FCSTD DOCUMENT  (FreeCAD 1.0R39319 (Git))
Label: arm3
License: All rights reserved
LicenseURL: https://en.wikipedia.org/wiki/All_rights_reserved
objects: Sketcher::SketchObject×1, PartDesign::Body×1
note: 3 computed .brp shape members not serialized (recipe doc carries the construction recipe); baked Part::Feature solids carry a one-line shape summary decoded from their .brp

FEATURE [Sketcher::SketchObject] Sketch
  ArcFitTolerance = 1e-06
  AttachmentSupport = -> [XY_Plane]
  FullyConstrained = false
  MakeInternals = false
  MapMode = 5
  sketch-geometry (162):
    g0: LineSegment [constr] StartX=20.0632 StartY=2.83397e-05 StartZ=0 EndX=20.0632 EndY=-40 EndZ=0
    g1: Circle [constr] CenterX=20.0632 CenterY=-20 CenterZ=0 NormalX=0 NormalY=0 NormalZ=1 AngleXU=0 Radius=14
    g2: LineSegment [constr] StartX=20.0632 StartY=-20 StartZ=0 EndX=20.0632 EndY=380 EndZ=0
    g3: LineSegment [constr] StartX=20.0632 StartY=2.83397e-05 StartZ=0 EndX=20.0632 EndY=5.00004 EndZ=0
    g4: Circle CenterX=20.0632 CenterY=380 CenterZ=0 NormalX=0 NormalY=0 NormalZ=1 AngleXU=0 Radius=5
    g5: LineSegment [constr] StartX=20.0632 StartY=-20 StartZ=0 EndX=-4.93685 EndY=-20 EndZ=0
    g6: LineSegment [constr] StartX=20.0632 StartY=-20 StartZ=0 EndX=45.0632 EndY=-20 EndZ=0
    g7: Circle CenterX=20.0632 CenterY=380 CenterZ=0 NormalX=0 NormalY=0 NormalZ=1 AngleXU=0 Radius=2
    g8: LineSegment [constr] StartX=120.063 StartY=-20 StartZ=0 EndX=120.063 EndY=380 EndZ=0
    g9: Circle CenterX=120.063 CenterY=380 CenterZ=0 NormalX=0 NormalY=0 NormalZ=1 AngleXU=0 Radius=5
    g10: Circle CenterX=120.063 CenterY=380 CenterZ=0 NormalX=0 NormalY=0 NormalZ=1 AngleXU=0 Radius=2
    g11: LineSegment [constr] StartX=120.063 StartY=3.7e-05 StartZ=0 EndX=120.063 EndY=-40 EndZ=0
    g12: Circle [constr] CenterX=120.063 CenterY=-20 CenterZ=0 NormalX=0 NormalY=0 NormalZ=1 AngleXU=0 Radius=14
    g13: LineSegment [constr] StartX=120.063 StartY=-20 StartZ=0 EndX=95.0632 EndY=-20 EndZ=0
    g14: Circle [constr] CenterX=20.0632 CenterY=-20.0003 CenterZ=0 NormalX=0 NormalY=0 NormalZ=1 AngleXU=0 Radius=11
    g15: LineSegment [constr] StartX=20.0632 StartY=-20 StartZ=0 EndX=20.0632 EndY=-9.00027 EndZ=0
    g16: Circle CenterX=20.0632 CenterY=-9.00027 CenterZ=0 NormalX=0 NormalY=0 NormalZ=1 AngleXU=0 Radius=1.25
    g17: Circle CenterX=9.06345 CenterY=-20 CenterZ=0 NormalX=0 NormalY=0 NormalZ=1 AngleXU=0 Radius=1.25
    g18: Circle CenterX=20.0632 CenterY=-30.9997 CenterZ=0 NormalX=0 NormalY=0 NormalZ=1 AngleXU=0 Radius=1.25
    g19: Circle CenterX=31.0629 CenterY=-20 CenterZ=0 NormalX=0 NormalY=0 NormalZ=1 AngleXU=0 Radius=1.25
    g20: LineSegment [constr] StartX=120.063 StartY=-20 StartZ=0 EndX=145.063 EndY=-20 EndZ=0
    g21: Circle [constr] CenterX=120.063 CenterY=-20.0003 CenterZ=0 NormalX=0 NormalY=0 NormalZ=1 AngleXU=0 Radius=11
    g22: Circle CenterX=131.063 CenterY=-20 CenterZ=0 NormalX=0 NormalY=0 NormalZ=1 AngleXU=0 Radius=1.25
    g23: Circle CenterX=120.063 CenterY=-9.00027 CenterZ=0 NormalX=0 NormalY=0 NormalZ=1 AngleXU=0 Radius=1.25
    g24: Circle CenterX=109.063 CenterY=-20 CenterZ=0 NormalX=0 NormalY=0 NormalZ=1 AngleXU=0 Radius=1.25
    g25: Circle CenterX=120.063 CenterY=-30.9997 CenterZ=0 NormalX=0 NormalY=0 NormalZ=1 AngleXU=0 Radius=1.25
    g26: LineSegment [constr] StartX=99.9621 StartY=66.1 StartZ=0 EndX=140.162 EndY=66.1 EndZ=0
    g27: LineSegment [constr] StartX=140.162 StartY=66.1 StartZ=0 EndX=140.162 EndY=5.00003 EndZ=0
    g28: LineSegment [constr] StartX=120.062 StartY=60.5 StartZ=0 EndX=134.562 EndY=60.5 EndZ=0
    g29: LineSegment StartX=134.562 StartY=60.5 StartZ=0 EndX=105.562 EndY=60.5 EndZ=0
    g30: LineSegment StartX=134.562 StartY=60.5 StartZ=0 EndX=134.562 EndY=5.00003 EndZ=0
    g31: Circle CenterX=131.062 CenterY=63.3 CenterZ=0 NormalX=0 NormalY=0 NormalZ=1 AngleXU=0 Radius=1.25
    g32: Circle CenterX=137.362 CenterY=36 CenterZ=0 NormalX=0 NormalY=0 NormalZ=1 AngleXU=0 Radius=1.25
    g33: Circle CenterX=137.362 CenterY=58 CenterZ=0 NormalX=0 NormalY=0 NormalZ=1 AngleXU=0 Radius=1.25
    g34: LineSegment [constr] StartX=102.762 StartY=36 StartZ=0 EndX=137.362 EndY=36 EndZ=0
    g35: Circle [constr] CenterX=120.062 CenterY=18 CenterZ=0 NormalX=0 NormalY=0 NormalZ=1 AngleXU=0 Radius=14
    g36: Circle CenterX=137.362 CenterY=14 CenterZ=0 NormalX=0 NormalY=0 NormalZ=1 AngleXU=0 Radius=1.25
    g37: ArcOfCircle CenterX=120.062 CenterY=18 CenterZ=0 NormalX=0 NormalY=0 NormalZ=1 AngleXU=0 Radius=14 StartAngle=4.33214 EndAngle=5.09264
    g38: LineSegment [constr] StartX=140.162 StartY=5.00003 StartZ=0 EndX=134.562 EndY=5.00003 EndZ=0
    g39: LineSegment StartX=125.258 StartY=5.00003 StartZ=0 EndX=134.562 EndY=5.00003 EndZ=0
    g40: LineSegment StartX=105.562 StartY=60.5 StartZ=0 EndX=105.562 EndY=5.00004 EndZ=0
    g41: LineSegment [constr] StartX=99.9621 StartY=5.00004 StartZ=0 EndX=99.9621 EndY=66.1 EndZ=0
    g42: Circle CenterX=102.762 CenterY=36 CenterZ=0 NormalX=0 NormalY=0 NormalZ=1 AngleXU=0 Radius=1.25
    g43: Circle CenterX=102.762 CenterY=58 CenterZ=0 NormalX=0 NormalY=0 NormalZ=1 AngleXU=0 Radius=1.25
    g44: Circle CenterX=109.062 CenterY=63.3 CenterZ=0 NormalX=0 NormalY=0 NormalZ=1 AngleXU=0 Radius=1.25
    g45: Circle CenterX=102.762 CenterY=14 CenterZ=0 NormalX=0 NormalY=0 NormalZ=1 AngleXU=0 Radius=1.25
    g46: LineSegment [constr] StartX=99.9621 StartY=5.00004 StartZ=0 EndX=105.562 EndY=5.00004 EndZ=0
    g47: LineSegment StartX=105.562 StartY=5.00004 StartZ=0 EndX=114.866 EndY=5.00004 EndZ=0
    g48: LineSegment [constr] StartX=-0.037918 StartY=66.1 StartZ=0 EndX=40.1621 EndY=66.1 EndZ=0
    g49: LineSegment [constr] StartX=40.1621 StartY=66.1 StartZ=0 EndX=40.1621 EndY=5.00003 EndZ=0
    g50: LineSegment [constr] StartX=20.0621 StartY=60.5 StartZ=0 EndX=34.5621 EndY=60.5 EndZ=0
    g51: LineSegment StartX=34.5621 StartY=60.5 StartZ=0 EndX=5.56208 EndY=60.5 EndZ=0
    g52: LineSegment StartX=34.5621 StartY=60.5 StartZ=0 EndX=34.5621 EndY=5.00003 EndZ=0
    g53: Circle CenterX=31.0621 CenterY=63.3 CenterZ=0 NormalX=0 NormalY=0 NormalZ=1 AngleXU=0 Radius=1.25
    g54: Circle CenterX=37.3621 CenterY=36 CenterZ=0 NormalX=0 NormalY=0 NormalZ=1 AngleXU=0 Radius=1.25
    g55: Circle CenterX=37.3621 CenterY=58 CenterZ=0 NormalX=0 NormalY=0 NormalZ=1 AngleXU=0 Radius=1.25
    g56: LineSegment [constr] StartX=2.76208 StartY=36 StartZ=0 EndX=37.3621 EndY=36 EndZ=0
    g57: Circle [constr] CenterX=20.0621 CenterY=18 CenterZ=0 NormalX=0 NormalY=0 NormalZ=1 AngleXU=0 Radius=14
    g58: Circle CenterX=37.3621 CenterY=14 CenterZ=0 NormalX=0 NormalY=0 NormalZ=1 AngleXU=0 Radius=1.25
    g59: ArcOfCircle CenterX=20.0621 CenterY=18 CenterZ=0 NormalX=0 NormalY=0 NormalZ=1 AngleXU=0 Radius=14 StartAngle=4.33214 EndAngle=5.09264
    g60: LineSegment [constr] StartX=40.1621 StartY=5.00003 StartZ=0 EndX=34.5621 EndY=5.00003 EndZ=0
    g61: LineSegment StartX=25.2582 StartY=5.00003 StartZ=0 EndX=34.5621 EndY=5.00003 EndZ=0
    g62: LineSegment StartX=5.56208 StartY=60.5 StartZ=0 EndX=5.56208 EndY=5.00004 EndZ=0
    g63: LineSegment [constr] StartX=-0.037918 StartY=5.00004 StartZ=0 EndX=-0.037918 EndY=66.1 EndZ=0
    g64: Circle CenterX=2.76208 CenterY=36 CenterZ=0 NormalX=0 NormalY=0 NormalZ=1 AngleXU=0 Radius=1.25
    g65: Circle CenterX=2.76208 CenterY=58 CenterZ=0 NormalX=0 NormalY=0 NormalZ=1 AngleXU=0 Radius=1.25
    g66: Circle CenterX=9.06208 CenterY=63.3 CenterZ=0 NormalX=0 NormalY=0 NormalZ=1 AngleXU=0 Radius=1.25
    g67: Circle CenterX=2.76208 CenterY=14 CenterZ=0 NormalX=0 NormalY=0 NormalZ=1 AngleXU=0 Radius=1.25
    g68: LineSegment [constr] StartX=-0.037918 StartY=5.00004 StartZ=0 EndX=5.56208 EndY=5.00004 EndZ=0
    g69: LineSegment StartX=5.56208 StartY=5.00004 StartZ=0 EndX=14.8659 EndY=5.00004 EndZ=0
    g70: LineSegment [constr] StartX=120.063 StartY=-20 StartZ=0 EndX=220.063 EndY=-20 EndZ=0
    g71: LineSegment [constr] StartX=220.063 StartY=0.00034 StartZ=0 EndX=220.063 EndY=-39.9997 EndZ=0
    g72: Circle [constr] CenterX=220.063 CenterY=-19.9997 CenterZ=0 NormalX=0 NormalY=0 NormalZ=1 AngleXU=0 Radius=14
    g73: LineSegment [constr] StartX=220.063 StartY=-19.9997 StartZ=0 EndX=220.063 EndY=380.001 EndZ=0
    g74: ArcOfCircle CenterX=220.063 CenterY=380.001 CenterZ=0 NormalX=0 NormalY=0 NormalZ=1 AngleXU=0 Radius=25 StartAngle=0 EndAngle=1e-06
    g75: Circle CenterX=220.063 CenterY=380.001 CenterZ=0 NormalX=0 NormalY=0 NormalZ=1 AngleXU=0 Radius=5
    g76: LineSegment [constr] StartX=220.063 StartY=-19.9997 StartZ=0 EndX=245.063 EndY=-19.9997 EndZ=0
    g77: LineSegment [constr] StartX=220.063 StartY=-19.9997 StartZ=0 EndX=195.063 EndY=-19.9997 EndZ=0
    g78: Circle CenterX=220.063 CenterY=-19.9997 CenterZ=0 NormalX=0 NormalY=0 NormalZ=1 AngleXU=0 Radius=5
    g79: Circle CenterX=220.063 CenterY=380.001 CenterZ=0 NormalX=0 NormalY=0 NormalZ=1 AngleXU=0 Radius=2
    g80: Circle CenterX=220.063 CenterY=-19.9997 CenterZ=0 NormalX=0 NormalY=0 NormalZ=1 AngleXU=0 Radius=2
    g81: LineSegment [constr] StartX=320.063 StartY=0.00034 StartZ=0 EndX=320.063 EndY=-39.9997 EndZ=0
    g82: Circle [constr] CenterX=320.063 CenterY=-19.9997 CenterZ=0 NormalX=0 NormalY=0 NormalZ=1 AngleXU=0 Radius=14
    g83: LineSegment [constr] StartX=320.063 StartY=-19.9997 StartZ=0 EndX=320.063 EndY=380.001 EndZ=0
    g84: ArcOfCircle CenterX=320.063 CenterY=380.001 CenterZ=0 NormalX=0 NormalY=0 NormalZ=1 AngleXU=0 Radius=25 StartAngle=1e-16 EndAngle=1e-06
    g85: Circle CenterX=320.063 CenterY=380.001 CenterZ=0 NormalX=0 NormalY=0 NormalZ=1 AngleXU=0 Radius=5
    g86: LineSegment [constr] StartX=320.063 StartY=-19.9997 StartZ=0 EndX=345.063 EndY=-19.9997 EndZ=0
    g87: LineSegment [constr] StartX=320.063 StartY=-19.9997 StartZ=0 EndX=295.063 EndY=-19.9997 EndZ=0
    g88: Circle CenterX=320.063 CenterY=-19.9997 CenterZ=0 NormalX=0 NormalY=0 NormalZ=1 AngleXU=0 Radius=5
    g89: Circle CenterX=320.063 CenterY=380.001 CenterZ=0 NormalX=0 NormalY=0 NormalZ=1 AngleXU=0 Radius=2
    g90: Circle CenterX=320.063 CenterY=-19.9997 CenterZ=0 NormalX=0 NormalY=0 NormalZ=1 AngleXU=0 Radius=2
    g91: Circle CenterX=231.063 CenterY=-19.9997 CenterZ=0 NormalX=0 NormalY=0 NormalZ=1 AngleXU=0 Radius=1.25
    g92: Circle [constr] CenterX=220.063 CenterY=-20 CenterZ=0 NormalX=0 NormalY=0 NormalZ=1 AngleXU=0 Radius=11
    g93: Circle CenterX=220.063 CenterY=-8.99996 CenterZ=0 NormalX=0 NormalY=0 NormalZ=1 AngleXU=0 Radius=1.25
    g94: Circle CenterX=209.063 CenterY=-19.9997 CenterZ=0 NormalX=0 NormalY=0 NormalZ=1 AngleXU=0 Radius=1.25
    g95: Circle CenterX=220.063 CenterY=-30.9994 CenterZ=0 NormalX=0 NormalY=0 NormalZ=1 AngleXU=0 Radius=1.25
    g96: Circle [constr] CenterX=320.063 CenterY=-19.9997 CenterZ=0 NormalX=0 NormalY=0 NormalZ=1 AngleXU=0 Radius=11
    g97: Circle CenterX=331.063 CenterY=-19.9994 CenterZ=0 NormalX=0 NormalY=0 NormalZ=1 AngleXU=0 Radius=1.25
    g98: Circle CenterX=320.063 CenterY=-8.99966 CenterZ=0 NormalX=0 NormalY=0 NormalZ=1 AngleXU=0 Radius=1.25
    g99: Circle CenterX=309.063 CenterY=-19.9994 CenterZ=0 NormalX=0 NormalY=0 NormalZ=1 AngleXU=0 Radius=1.25
    g100: Circle CenterX=320.063 CenterY=-30.9991 CenterZ=0 NormalX=0 NormalY=0 NormalZ=1 AngleXU=0 Radius=1.25
    g101: LineSegment [constr] StartX=-4.93685 StartY=180.003 StartZ=0 EndX=45.0528 EndY=180.003 EndZ=0
    g102: LineSegment [constr] StartX=-4.93685 StartY=180.003 StartZ=0 EndX=-34.9368 EndY=180.003 EndZ=0
    g103: ArcOfCircle CenterX=120.063 CenterY=380 CenterZ=0 NormalX=0 NormalY=0 NormalZ=1 AngleXU=0 Radius=25 StartAngle=6.28319 EndAngle=6.28319
    g104: LineSegment [constr] StartX=-4.93685 StartY=-20 StartZ=0 EndX=-34.9368 EndY=-20 EndZ=0
    g105: LineSegment [constr] StartX=-4.93685 StartY=380.208 StartZ=0 EndX=-34.9368 EndY=380.208 EndZ=0
    g106: LineSegment [constr] StartX=-34.9368 StartY=180.003 StartZ=0 EndX=-34.9368 EndY=380.208 EndZ=0
    g107: LineSegment [constr] StartX=-34.9368 StartY=180.003 StartZ=0 EndX=-34.9368 EndY=-20 EndZ=0
    g108: LineSegment [constr] StartX=-34.9368 StartY=280.106 StartZ=0 EndX=-4.93685 EndY=280.106 EndZ=0
    g109: LineSegment [constr] StartX=-4.93685 StartY=280.106 StartZ=0 EndX=45.058 EndY=280.106 EndZ=0
    g110: LineSegment [constr] StartX=-34.9368 StartY=80.0017 StartZ=0 EndX=-4.93685 EndY=80.0017 EndZ=0
    g111: LineSegment [constr] StartX=-4.93685 StartY=80.0017 StartZ=0 EndX=45.0476 EndY=80.0017 EndZ=0
    g112: LineSegment [constr] StartX=-4.93685 StartY=280.106 StartZ=0 EndX=0.0631523 EndY=280.106 EndZ=0
    g113: LineSegment [constr] StartX=0.0631523 StartY=280.106 StartZ=0 EndX=0.0631523 EndY=180.003 EndZ=0
    g114: LineSegment [constr] StartX=0.0631523 StartY=180.003 StartZ=0 EndX=0.0631523 EndY=80.0017 EndZ=0
    g115: LineSegment [constr] StartX=45.058 StartY=280.106 StartZ=0 EndX=40.058 EndY=280.106 EndZ=0
    g116: LineSegment [constr] StartX=40.058 StartY=280.106 StartZ=0 EndX=40.058 EndY=180.003 EndZ=0
    g117: LineSegment [constr] StartX=40.058 StartY=180.003 StartZ=0 EndX=40.058 EndY=80.0017 EndZ=0
    g118: Circle CenterX=0.0631523 CenterY=280.106 CenterZ=0 NormalX=0 NormalY=0 NormalZ=1 AngleXU=0 Radius=1.5
    g119: Circle CenterX=40.058 CenterY=280.106 CenterZ=0 NormalX=0 NormalY=0 NormalZ=1 AngleXU=0 Radius=1.5
    g120: Circle CenterX=0.0631523 CenterY=180.003 CenterZ=0 NormalX=0 NormalY=0 NormalZ=1 AngleXU=0 Radius=1.5
    g121: Circle CenterX=40.058 CenterY=180.003 CenterZ=0 NormalX=0 NormalY=0 NormalZ=1 AngleXU=0 Radius=1.5
    g122: Circle CenterX=0.0631523 CenterY=80.0017 CenterZ=0 NormalX=0 NormalY=0 NormalZ=1 AngleXU=0 Radius=1.5
    g123: Circle CenterX=40.058 CenterY=80.0017 CenterZ=0 NormalX=0 NormalY=0 NormalZ=1 AngleXU=0 Radius=1.5
    g124: Circle CenterX=100.063 CenterY=280.106 CenterZ=0 NormalX=0 NormalY=0 NormalZ=1 AngleXU=0 Radius=1.5
    g125: Circle CenterX=140.058 CenterY=280.106 CenterZ=0 NormalX=0 NormalY=0 NormalZ=1 AngleXU=0 Radius=1.5
    g126: Circle CenterX=100.063 CenterY=180.003 CenterZ=0 NormalX=0 NormalY=0 NormalZ=1 AngleXU=0 Radius=1.5
    g127: Circle CenterX=140.058 CenterY=180.003 CenterZ=0 NormalX=0 NormalY=0 NormalZ=1 AngleXU=0 Radius=1.5
    g128: Circle CenterX=100.063 CenterY=80.0017 CenterZ=0 NormalX=0 NormalY=0 NormalZ=1 AngleXU=0 Radius=1.5
    g129: Circle CenterX=140.058 CenterY=80.0017 CenterZ=0 NormalX=0 NormalY=0 NormalZ=1 AngleXU=0 Radius=1.5
    g130: Circle CenterX=200.063 CenterY=280.106 CenterZ=0 NormalX=0 NormalY=0 NormalZ=1 AngleXU=0 Radius=1.5
    g131: Circle CenterX=240.058 CenterY=280.106 CenterZ=0 NormalX=0 NormalY=0 NormalZ=1 AngleXU=0 Radius=1.5
    g132: Circle CenterX=200.063 CenterY=180.003 CenterZ=0 NormalX=0 NormalY=0 NormalZ=1 AngleXU=0 Radius=1.5
    g133: Circle CenterX=240.058 CenterY=180.003 CenterZ=0 NormalX=0 NormalY=0 NormalZ=1 AngleXU=0 Radius=1.5
    g134: Circle CenterX=200.063 CenterY=80.0017 CenterZ=0 NormalX=0 NormalY=0 NormalZ=1 AngleXU=0 Radius=1.5
    g135: Circle CenterX=240.058 CenterY=80.0017 CenterZ=0 NormalX=0 NormalY=0 NormalZ=1 AngleXU=0 Radius=1.5
    g136: Circle CenterX=300.063 CenterY=280.106 CenterZ=0 NormalX=0 NormalY=0 NormalZ=1 AngleXU=0 Radius=1.5
    g137: Circle CenterX=340.058 CenterY=280.106 CenterZ=0 NormalX=0 NormalY=0 NormalZ=1 AngleXU=0 Radius=1.5
    g138: Circle CenterX=300.063 CenterY=180.003 CenterZ=0 NormalX=0 NormalY=0 NormalZ=1 AngleXU=0 Radius=1.5
    g139: Circle CenterX=340.058 CenterY=180.003 CenterZ=0 NormalX=0 NormalY=0 NormalZ=1 AngleXU=0 Radius=1.5
    g140: Circle CenterX=300.063 CenterY=80.0017 CenterZ=0 NormalX=0 NormalY=0 NormalZ=1 AngleXU=0 Radius=1.5
    g141: Circle CenterX=340.058 CenterY=80.0017 CenterZ=0 NormalX=0 NormalY=0 NormalZ=1 AngleXU=0 Radius=1.5
    g142: Circle CenterX=120.063 CenterY=-19.9997 CenterZ=0 NormalX=0 NormalY=0 NormalZ=1 AngleXU=0 Radius=5
    g143: Circle CenterX=120.063 CenterY=-19.9997 CenterZ=0 NormalX=0 NormalY=0 NormalZ=1 AngleXU=0 Radius=2
    g144: Circle CenterX=20.0632 CenterY=-19.9997 CenterZ=0 NormalX=0 NormalY=0 NormalZ=1 AngleXU=0 Radius=5
    g145: Circle CenterX=20.0632 CenterY=-19.9997 CenterZ=0 NormalX=0 NormalY=0 NormalZ=1 AngleXU=0 Radius=2
    g146: ArcOfCircle CenterX=20.0632 CenterY=-19.9997 CenterZ=0 NormalX=0 NormalY=0 NormalZ=1 AngleXU=0 Radius=25 StartAngle=3.14159 EndAngle=6.28319
    g147: ArcOfCircle CenterX=20.0632 CenterY=380 CenterZ=0 NormalX=0 NormalY=0 NormalZ=1 AngleXU=0 Radius=25 StartAngle=8.3e-15 EndAngle=3.14159
    g148: LineSegment StartX=-4.93685 StartY=-19.9997 StartZ=0 EndX=-4.93685 EndY=380 EndZ=0
    g149: LineSegment StartX=45.0632 StartY=-19.9997 StartZ=0 EndX=45.0632 EndY=380 EndZ=0
    g150: ArcOfCircle CenterX=120.063 CenterY=-19.9997 CenterZ=0 NormalX=0 NormalY=0 NormalZ=1 AngleXU=0 Radius=25 StartAngle=3.14159 EndAngle=6.28319
    g151: ArcOfCircle CenterX=120.063 CenterY=380 CenterZ=0 NormalX=0 NormalY=0 NormalZ=1 AngleXU=0 Radius=25 StartAngle=0 EndAngle=3.14159
    g152: LineSegment StartX=95.0632 StartY=-19.9997 StartZ=0 EndX=95.0632 EndY=380 EndZ=0
    g153: LineSegment StartX=145.063 StartY=-19.9997 StartZ=0 EndX=145.063 EndY=380 EndZ=0
    g154: ArcOfCircle CenterX=220.063 CenterY=380.001 CenterZ=0 NormalX=0 NormalY=0 NormalZ=1 AngleXU=0 Radius=25 StartAngle=3e-15 EndAngle=3.14159
    g155: ArcOfCircle CenterX=220.063 CenterY=-19.9997 CenterZ=0 NormalX=0 NormalY=0 NormalZ=1 AngleXU=0 Radius=25 StartAngle=3.14159 EndAngle=6.28319
    g156: LineSegment StartX=245.063 StartY=380.001 StartZ=0 EndX=245.063 EndY=-19.9997 EndZ=0
    g157: LineSegment StartX=195.063 StartY=380.001 StartZ=0 EndX=195.063 EndY=-19.9997 EndZ=0
    g158: ArcOfCircle CenterX=320.063 CenterY=380.001 CenterZ=0 NormalX=0 NormalY=0 NormalZ=1 AngleXU=0 Radius=25 StartAngle=9e-16 EndAngle=3.14159
    g159: ArcOfCircle CenterX=320.063 CenterY=-19.9997 CenterZ=0 NormalX=0 NormalY=0 NormalZ=1 AngleXU=0 Radius=25 StartAngle=3.14159 EndAngle=6.28319
    g160: LineSegment StartX=345.063 StartY=380.001 StartZ=0 EndX=345.063 EndY=-19.9997 EndZ=0
    g161: LineSegment StartX=295.063 StartY=380.001 StartZ=0 EndX=295.063 EndY=-19.9997 EndZ=0
  constraints (279):
    c: Distance(g0) = 40
    c: Vertical(g0)
    c: Diameter(g1) = 28
    c: Symmetric(g0,g0,g1)
    c: Distance(g2) = 400
    c: Coincident(g2,g1)
    c: Vertical(g2)
    c: Coincident(g3,g0)
    c: Vertical(g3)
    c: Diameter(g4) = 10
    c: Coincident(g4,g2)
    c: Coincident(g5,g1)
    c: Horizontal(g5)
    c: Coincident(g6,g1)
    c: Horizontal(g6)
    c: PointOnObject(g104,g5)
    c: Diameter(g7) = 4
    c: Coincident(g7,g2)
    c: Vertical(g11)
    c: Diameter(g12) = 28
    c: Symmetric(g11,g11,g12)
    c: Coincident(g8,g12)
    c: Vertical(g8)
    c: Coincident(g9,g8)
    c: Coincident(g13,g12)
    c: Horizontal(g13)
    c: Diameter(g10) = 4
    c: Coincident(g10,g8)
    c: Diameter(g14) = 22
    c: Coincident(g15,g1)
    c: PointOnObject(g15,g14)
    c: Vertical(g15)
    c: Diameter(g16) = 2.5
    c: Coincident(g16,g15)
    c: Diameter(g17) = 2.5
    c: Diameter(g18) = 2.5
    c: Diameter(g19) = 2.5
    c: Horizontal(g20)
    c: Diameter(g21) = 22
    c: Diameter(g23) = 2.5
    c: Diameter(g24) = 2.5
    c: Diameter(g25) = 2.5
    c: Diameter(g22) = 2.5
    c: Coincident(g26,g27)
    c: Coincident(g41,g26)
    c: Horizontal(g26)
    c: Vertical(g27)
    c: Vertical(g41)
    c: Distance(g27,g41) = 40.2
    c: Distance(g26,g41) = 61.1
    c: Diameter(g37) = 28
    c: Horizontal(g28)
    c: Coincident(g29,g28)
    c: Horizontal(g29)
    c: Coincident(g40,g29)
    c: Vertical(g40)
    c: Coincident(g30,g28)
    c: Vertical(g30)
    c: Diameter(g31) = 2.5
    c: Equal(g31,g44)
    c: Equal(g31,g36)
    c: Equal(g31,g45)
    c: Equal(g31,g42)
    c: Equal(g31,g43)
    c: Equal(g31,g33)
    c: Equal(g31,g32)
    c: Coincident(g35,g37)
    c: PointOnObject(g37,g35)
    c: Coincident(g34,g42)
    c: Coincident(g34,g32)
    c: Horizontal(g34)
    c: Coincident(g46,g41)
    c: Coincident(g46,g40)
    c: Horizontal(g46)
    c: Coincident(g38,g27)
    c: Coincident(g38,g30)
    c: Horizontal(g38)
    c: Coincident(g39,g37)
    c: Coincident(g39,g30)
    c: Horizontal(g39)
    c: Coincident(g47,g40)
    c: Coincident(g47,g37)
    c: Horizontal(g47)
    c: DistanceY(g35,g8) = 362
    c: Coincident(g48,g49)
    c: Coincident(g63,g48)
    c: Horizontal(g48)
    c: Vertical(g49)
    c: Vertical(g63)
    c: Distance(g49,g63) = 40.2
    c: Distance(g48,g63) = 61.1
    c: Diameter(g59) = 28
    c: Horizontal(g50)
    c: Coincident(g51,g50)
    c: Horizontal(g51)
    c: Coincident(g62,g51)
    c: Vertical(g62)
    c: Coincident(g52,g50)
    c: Vertical(g52)
    c: Diameter(g53) = 2.5
    c: Equal(g53,g66)
    c: Equal(g53,g58)
    c: Equal(g53,g67)
    c: Equal(g53,g64)
    c: Equal(g53,g65)
    c: Equal(g53,g55)
    c: Equal(g53,g54)
    c: Coincident(g57,g59)
    c: PointOnObject(g59,g57)
    c: Coincident(g56,g64)
    c: Coincident(g56,g54)
    c: Horizontal(g56)
    c: Coincident(g68,g63)
    c: Coincident(g68,g62)
    c: Horizontal(g68)
    c: Coincident(g60,g49)
    c: Coincident(g60,g52)
    c: Horizontal(g60)
    c: Coincident(g61,g59)
    c: Coincident(g61,g52)
    c: Horizontal(g61)
    c: Coincident(g69,g62)
    c: Coincident(g69,g59)
    c: Horizontal(g69)
    c: Distance(g70) = 100
    c: Horizontal(g70)
    c: Vertical(g71)
    c: Diameter(g72) = 28
    c: Symmetric(g71,g71,g72)
    c: Coincident(g73,g72)
    c: Vertical(g73)
    c: Diameter(g74) = 50
    c: Coincident(g74,g73)
    c: Coincident(g75,g73)
    c: Coincident(g76,g72)
    c: Horizontal(g76)
    c: Coincident(g77,g72)
    c: Horizontal(g77)
    c: Diameter(g78) = 10
    c: Diameter(g79) = 4
    c: Coincident(g79,g73)
    c: Diameter(g80) = 4
    c: Coincident(g80,g72)
    c: Vertical(g81)
    c: Diameter(g82) = 28
    c: Symmetric(g81,g81,g82)
    c: Coincident(g83,g82)
    c: Vertical(g83)
    c: Diameter(g84) = 50
    c: Coincident(g84,g83)
    c: Coincident(g85,g83)
    c: Coincident(g86,g82)
    c: Horizontal(g86)
    c: Coincident(g87,g82)
    c: Horizontal(g87)
    c: Diameter(g88) = 10
    c: Diameter(g89) = 4
    c: Coincident(g89,g83)
    c: Diameter(g90) = 4
    c: Coincident(g90,g82)
    c: Diameter(g92) = 22
    c: Diameter(g93) = 2.5
    c: Diameter(g94) = 2.5
    c: Diameter(g95) = 2.5
    c: Diameter(g91) = 2.5
    c: Diameter(g96) = 22
    c: Diameter(g98) = 2.5
    c: Diameter(g99) = 2.5
    c: Diameter(g100) = 2.5
    c: Diameter(g97) = 2.5
    c: Horizontal(g101)
    c: Distance(g102) = 30
    c: Horizontal(g102)
    c: Coincident(g102,g101)
    c: Distance(g104) = 30
    c: Horizontal(g104)
    c: Distance(g105) = 30
    c: Horizontal(g105)
    c: Coincident(g106,g102)
    c: Coincident(g106,g105)
    c: Vertical(g106)
    c: Coincident(g107,g102)
    c: Coincident(g107,g104)
    c: Symmetric(g106,g106,g108)
    c: Horizontal(g108)
    c: Coincident(g109,g108)
    c: Horizontal(g109)
    c: Symmetric(g107,g107,g110)
    c: Horizontal(g110)
    c: Coincident(g111,g110)
    c: Horizontal(g111)
    c: Distance(g112) = 5
    c: Coincident(g112,g108)
    c: PointOnObject(g112,g109)
    c: Coincident(g113,g112)
    c: PointOnObject(g113,g101)
    c: Vertical(g113)
    c: Coincident(g114,g113)
    c: PointOnObject(g114,g111)
    c: Vertical(g114)
    c: Distance(g115) = 5
    c: Horizontal(g115)
    c: Coincident(g115,g109)
    c: Coincident(g116,g115)
    c: PointOnObject(g116,g101)
    c: Vertical(g116)
    c: Coincident(g117,g116)
    c: PointOnObject(g117,g111)
    c: Vertical(g117)
    c: Coincident(g118,g112)
    c: Diameter(g118) = 3
    c: Coincident(g119,g115)
    c: Coincident(g120,g113)
    c: Coincident(g121,g116)
    c: Coincident(g122,g114)
    c: Coincident(g123,g117)
    c: Equal(g118,g119)
    c: Equal(g118,g120)
    c: Equal(g120,g121)
    c: Equal(g120,g122)
    c: Equal(g122,g123)
    c: Diameter(g124) = 3
    c: Diameter(g130) = 3
    c: Diameter(g136) = 3
    c: Equal(g124,g125)
    c: Equal(g130,g131)
    c: Equal(g136,g137)
    c: Equal(g124,g126)
    c: Equal(g130,g132)
    c: Equal(g136,g138)
    c: Equal(g126,g127)
    c: Equal(g132,g133)
    c: Equal(g138,g139)
    c: Equal(g126,g128)
    c: Equal(g132,g134)
    c: Equal(g138,g140)
    c: Equal(g128,g129)
    c: Equal(g134,g135)
    c: Equal(g140,g141)
    c: Diameter(g142) = 10
    c: Diameter(g144) = 10
    c: Diameter(g143) = 4
    c: Diameter(g145) = 4
    c: Tangent(g146,g148) = 1.5708
    c: Tangent(g146,g149) = -1.5708
    c: Tangent(g147,g148) = 1.5708
    c: Tangent(g147,g149) = -1.5708
    c: Equal(g146,g147)
    c: Vertical(g149)
    c: Radius(g146) = 25
    c: Coincident(g146,g144)
    c: Coincident(g147,g2)
    c: Tangent(g150,g152) = 1.5708
    c: Tangent(g150,g153) = -1.5708
    c: Tangent(g151,g152) = 1.5708
    c: Tangent(g151,g153) = -1.5708
    c: Equal(g150,g151)
    c: Vertical(g153)
    c: Radius(g150) = 25
    c: Coincident(g150,g142)
    c: Coincident(g151,g103)
    c: Tangent(g154,g156) = 1.5708
    c: Tangent(g154,g157) = -1.5708
    c: Tangent(g155,g156) = 1.5708
    c: Tangent(g155,g157) = -1.5708
    c: Equal(g154,g155)
    c: Vertical(g157)
    c: Radius(g154) = 25
    c: Coincident(g154,g73)
    c: Coincident(g155,g78)
    c: Tangent(g158,g160) = 1.5708
    c: Tangent(g158,g161) = -1.5708
    c: Tangent(g159,g160) = 1.5708
    c: Tangent(g159,g161) = -1.5708
    c: Equal(g158,g159)
    c: Vertical(g161)
    c: Radius(g158) = 25
    c: Coincident(g158,g83)
    c: Coincident(g159,g88)
FEATURE [PartDesign::Body] Body
  AllowCompound = false
  Group = -> [Sketch]
  Origin = -> Origin
